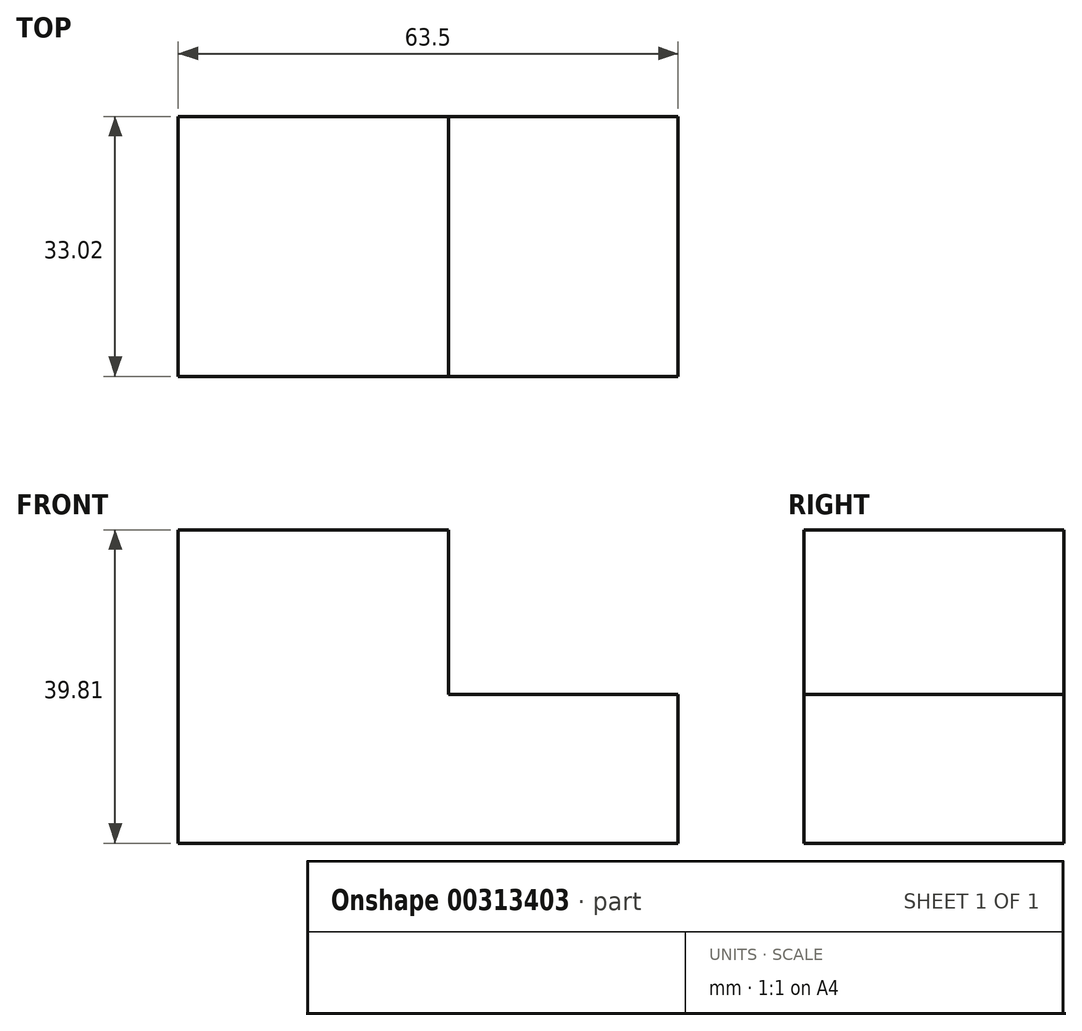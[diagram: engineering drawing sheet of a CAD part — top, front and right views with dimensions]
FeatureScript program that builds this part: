
annotation { "Feature Type Name" : "Feature", "Feature Type Description" : "" }
export const myFeature = defineFeature(function(context is Context, id is Id, definition is map)
    precondition{}
    {
        {
            var Q0;
            Q0=qCreatedBy(makeId("Front.planeOp"),FACE);
            var sketch = newSketch(context, id + "F0", { "sketchPlane" : qUnion([Q0])});
            skLineSegment(sketch, "E0", {"start": v(-44.26, -20.27) * mm, "end": v(-9.9, -20.27) * mm});
            skLineSegment(sketch, "E1", {"start": v(-44.26, -20.27) * mm, "end": v(-44.26, -52.46) * mm});
            skLineSegment(sketch, "E2", {"start": v(-44.26, -52.46) * mm, "end": v(19.24, -52.46) * mm});
            skLineSegment(sketch, "E3", {"start": v(19.24, -52.46) * mm, "end": v(19.24, -33.58) * mm});
            skLineSegment(sketch, "E4", {"start": v(19.24, -33.58) * mm, "end": v(-9.9, -33.58) * mm});
            skLineSegment(sketch, "E5", {"start": v(-9.9, -33.58) * mm, "end": v(-9.9, -20.27) * mm});
            skSolve(sketch);
        }
        {
            var Q0;
            Q0=makeQuery(id+"F0.imprint","IMPRINT",FACE,{"disambiguationData":[TD([[makeQuery(id+"F0.imprint","IMPRINT",EDGE,{"derivedFrom":sQuery(id+"F0.wireOp",EDGE,"E0")}),-1.0]])]});
            extrude(context, id + "F1", {"entities" : qUnion([Q0]), "oppositeDirection" : true, "depth" : 25.4 * mm});
        }
        {
            var Q0;
            Q0=makeQuery(id+"F1.opExtrude","SWEPT_FACE",FACE,{"disambiguationData":[OSD([sQuery(id+"F0.wireOp",EDGE,"E0")])]});
            extrude(context, id + "F2", {"entities" : qUnion([Q0]), "operationType" : NewBodyOperationType.ADD, "depth" : 7.62 * mm});
        }
        {
            var Q0;
            {var subQ0=sQuery(id+"F0.wireOp",EDGE,"E0");Q0=makeQuery(id+"F2.boolean.opBoolean","MERGE",FACE,{"derivedFrom":[makeQuery(id+"F1.opExtrude","CAP_FACE",FACE,{"disambiguationData":[OSD([subQ0,sQuery(id+"F0.wireOp",EDGE,"E1"),sQuery(id+"F0.wireOp",EDGE,"E2"),sQuery(id+"F0.wireOp",EDGE,"E3"),sQuery(id+"F0.wireOp",EDGE,"E4"),sQuery(id+"F0.wireOp",EDGE,"E5")])],"isStart":true}),makeQuery(id+"F2.opExtrude","SWEPT_FACE",FACE,{"disambiguationData":[OSD([subQ0]),TDD([makeQuery(id+"F1.opExtrude","CAP_EDGE",EDGE,{"disambiguationData":[OSD([subQ0])],"isStart":true})])]})]});}
            extrude(context, id + "F3", {"entities" : qUnion([Q0]), "operationType" : NewBodyOperationType.ADD, "depth" : 7.62 * mm});
        }
    });
